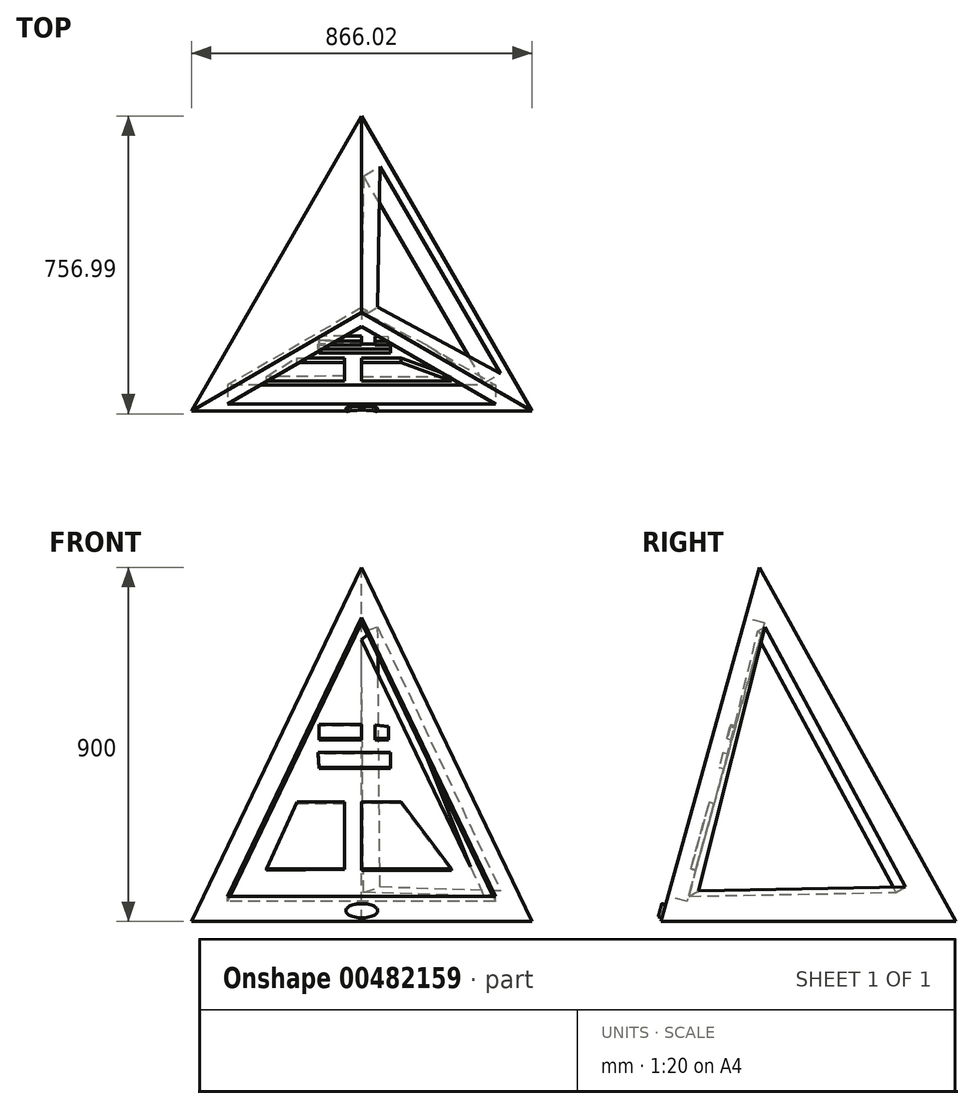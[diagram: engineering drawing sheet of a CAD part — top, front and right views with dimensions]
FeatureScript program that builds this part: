
annotation { "Feature Type Name" : "Feature", "Feature Type Description" : "" }
export const myFeature = defineFeature(function(context is Context, id is Id, definition is map)
    precondition{}
    {
        {
            var Q0;
            Q0=qCreatedBy(makeId("Top.planeOp"),FACE);
            var sketch = newSketch(context, id + "F0", { "sketchPlane" : qUnion([Q0])});
            skCircle(sketch, "E0.cCircle", {"center": v(0, 0) * mm, "radius": 250 * mm, "construction": true});
            skLineSegment(sketch, "E0.0", {"start": v(433.01, -250) * mm, "end": v(-433.01, -250) * mm});
            skLineSegment(sketch, "E0.1", {"start": v(-433.01, -250) * mm, "end": v(0, 500) * mm});
            skLineSegment(sketch, "E0.2", {"start": v(0, 500) * mm, "end": v(433.01, -250) * mm});
            skPoint(sketch, "E0.0.midPoint", {"position": v(0, -250) * mm});
            skSolve(sketch);
        }
        {
            var Q0;
            Q0=qCreatedBy(makeId("Top.planeOp"),FACE);
            cPlane(context, id + "F1", {"entities" : qUnion([Q0]), "cplaneType" : CPlaneType.OFFSET, "offset" : 400 * mm, "width" : 152.4 * mm, "height" : 152.4 * mm});
        }
        {
            var Q0;
            Q0=qCreatedBy(id+"F1.planeOp",FACE);
            cPlane(context, id + "F2", {"entities" : qUnion([Q0]), "cplaneType" : CPlaneType.OFFSET, "offset" : 500 * mm, "width" : 152.4 * mm, "height" : 152.4 * mm});
        }
        {
            var Q0;
            Q0=qCreatedBy(id+"F2.planeOp",FACE);
            var sketch = newSketch(context, id + "F3", { "sketchPlane" : qUnion([Q0])});
            skPoint(sketch, "E1.0", {"position": v(0, 0) * mm});
            skSolve(sketch);
        }
        {
            var Q0;
            Q0=makeQuery(id+"F0.imprint","IMPRINT",FACE,{"disambiguationData":[TD([[makeQuery(id+"F0.imprint","IMPRINT",EDGE,{"derivedFrom":sQuery(id+"F0.wireOp",EDGE,"E0.0")}),-1.0]])]});
            var Q1;
            Q1=sQuery(id+"F3.wireOp",VERTEX,"E1.0");
            loft(context, id + "F4", {"sheetProfilesArray" : [{ "sheetProfileEntities" : qUnion([Q0]) }, { "sheetProfileEntities" : qUnion([Q1]) }]});
        }
        {
            var Q0;
            {var subQ0=sQuery(id+"F0.wireOp",EDGE,"E0.0");var subQ1=sQuery(id+"F0.wireOp",EDGE,"E0.1");var subQ2=sQuery(id+"F0.wireOp",EDGE,"E0.2");Q0=makeQuery(id+"F4.opLoft","SWEPT_FACE",FACE,{"disambiguationData":[OSD([subQ0,subQ1,subQ2]),TDD([makeQuery(id+"F0.imprint","INTERSECT",VERTEX,{"derivedFrom":[subQ0,subQ2]}),makeQuery(id+"F0.imprint","INTERSECT",VERTEX,{"derivedFrom":[subQ0,subQ1]}),makeQuery(id+"F0.imprint","IMPRINT",EDGE,{"derivedFrom":subQ0})])]});}
            var sketch = newSketch(context, id + "F5", { "sketchPlane" : qUnion([Q0])});
            skLineSegment(sketch, "E2", {"start": v(0, 734.6) * mm, "end": v(-340.54, 0) * mm});
            skLineSegment(sketch, "E3", {"start": v(0, 734.6) * mm, "end": v(339.74, 0) * mm});
            skLineSegment(sketch, "E4", {"start": v(339.74, 0) * mm, "end": v(-340.54, 0) * mm});
            skSolve(sketch);
        }
        {
            var Q0;
            Q0 = qSketchRegion(id + "F5", true);
            extrude(context, id + "F6", {"entities" : qUnion([Q0]), "operationType" : NewBodyOperationType.REMOVE, "oppositeDirection" : true, "depth" : 50 * mm});
        }
        {
            var Q0;
            {var subQ0=sQuery(id+"F0.wireOp",EDGE,"E0.2");var subQ1=sQuery(id+"F0.wireOp",EDGE,"E0.1");var subQ2=sQuery(id+"F0.wireOp",EDGE,"E0.0");Q0=makeQuery(id+"F4.opLoft","SWEPT_FACE",FACE,{"disambiguationData":[OSD([subQ2,subQ1,subQ0]),TDD([makeQuery(id+"F0.imprint","INTERSECT",VERTEX,{"derivedFrom":[subQ2,subQ0]}),makeQuery(id+"F0.imprint","INTERSECT",VERTEX,{"derivedFrom":[subQ1,subQ0]}),makeQuery(id+"F0.imprint","IMPRINT",EDGE,{"derivedFrom":subQ0})])]});}
            var sketch = newSketch(context, id + "F7", { "sketchPlane" : qUnion([Q0])});
            skLineSegment(sketch, "E5", {"start": v(-116.62, 700.24) * mm, "end": v(-308.34, -33.85) * mm});
            skLineSegment(sketch, "E6", {"start": v(-308.34, -33.85) * mm, "end": v(291.14, 69.38) * mm});
            skLineSegment(sketch, "E7", {"start": v(291.14, 69.38) * mm, "end": v(-116.62, 700.24) * mm});
            skSolve(sketch);
        }
        {
            var Q0;
            Q0 = qSketchRegion(id + "F7", true);
            extrude(context, id + "F8", {"entities" : qUnion([Q0]), "operationType" : NewBodyOperationType.REMOVE, "oppositeDirection" : true, "depth" : 50 * mm});
        }
        {
            var Q0;
            Q0=makeQuery(id+"F6.boolean.opBoolean","COPY",FACE,{"derivedFrom":makeQuery(id+"F6.opExtrude","CAP_FACE",FACE,{"disambiguationData":[OSD([sQuery(id+"F5.wireOp",EDGE,"E2"),sQuery(id+"F5.wireOp",EDGE,"E3"),sQuery(id+"F5.wireOp",EDGE,"E4")])],"isStart":false})});
            var sketch = newSketch(context, id + "F9", { "sketchPlane" : qUnion([Q0])});
            skLineSegment(sketch, "E8", {"start": v(-241.35, 82.39) * mm, "end": v(-164.87, 258.78) * mm});
            skLineSegment(sketch, "E9", {"start": v(-164.87, 258.78) * mm, "end": v(-44.2, 258.78) * mm});
            skLineSegment(sketch, "E10", {"start": v(-44.2, 258.78) * mm, "end": v(-44.2, 84.15) * mm});
            skLineSegment(sketch, "E11", {"start": v(-44.2, 84.15) * mm, "end": v(-241.35, 82.39) * mm});
            skLineSegment(sketch, "E12", {"start": v(0, 258.78) * mm, "end": v(0, 82.39) * mm});
            skLineSegment(sketch, "E13", {"start": v(0, 82.39) * mm, "end": v(227.75, 82.39) * mm});
            skLineSegment(sketch, "E14", {"start": v(227.75, 82.39) * mm, "end": v(100.28, 258.78) * mm});
            skLineSegment(sketch, "E15", {"start": v(100.28, 258.78) * mm, "end": v(0, 258.78) * mm});
            skLineSegment(sketch, "E16", {"start": v(-108.78, 350.51) * mm, "end": v(73.08, 350.51) * mm});
            skLineSegment(sketch, "E17", {"start": v(73.08, 350.51) * mm, "end": v(73.08, 389.32) * mm});
            skLineSegment(sketch, "E18", {"start": v(73.08, 389.32) * mm, "end": v(-110.48, 389.32) * mm});
            skLineSegment(sketch, "E19", {"start": v(-110.48, 389.32) * mm, "end": v(-108.78, 350.51) * mm});
            skLineSegment(sketch, "E20", {"start": v(-108.78, 426.36) * mm, "end": v(0, 426.36) * mm});
            skLineSegment(sketch, "E21", {"start": v(0, 426.36) * mm, "end": v(0, 463.4) * mm});
            skLineSegment(sketch, "E22", {"start": v(0, 463.4) * mm, "end": v(-108.78, 463.4) * mm});
            skLineSegment(sketch, "E23", {"start": v(-108.78, 463.4) * mm, "end": v(-108.78, 426.36) * mm});
            skLineSegment(sketch, "E24", {"start": v(34, 461.64) * mm, "end": v(34, 426.36) * mm});
            skLineSegment(sketch, "E25", {"start": v(34, 426.36) * mm, "end": v(67.99, 426.36) * mm});
            skLineSegment(sketch, "E26", {"start": v(67.99, 426.36) * mm, "end": v(67.99, 458.12) * mm});
            skLineSegment(sketch, "E27", {"start": v(67.99, 458.12) * mm, "end": v(34, 461.64) * mm});
            skSolve(sketch);
        }
        {
            var Q0;
            {var subQ0=sQuery(id+"F0.wireOp",EDGE,"E0.0");var subQ1=sQuery(id+"F0.wireOp",EDGE,"E0.1");var subQ2=sQuery(id+"F0.wireOp",EDGE,"E0.2");Q0=makeQuery(id+"F4.opLoft","SWEPT_FACE",FACE,{"disambiguationData":[OSD([subQ0,subQ1,subQ2]),TDD([makeQuery(id+"F0.imprint","INTERSECT",VERTEX,{"derivedFrom":[subQ0,subQ2]}),makeQuery(id+"F0.imprint","INTERSECT",VERTEX,{"derivedFrom":[subQ0,subQ1]}),makeQuery(id+"F0.imprint","IMPRINT",EDGE,{"derivedFrom":subQ0})])]});}
            var sketch = newSketch(context, id + "F10", { "sketchPlane" : qUnion([Q0])});
            skEllipse(sketch, "E28", {"center": v(0, -39.74) * mm, "majorRadius": 40.13 * mm, "minorRadius": 17.28 * mm, "majorAxis": v(1, 0)});
            skSolve(sketch);
        }
        {
            var Q0;
            Q0 = qSketchRegion(id + "F10", true);
            extrude(context, id + "F11", {"entities" : qUnion([Q0]), "operationType" : NewBodyOperationType.ADD, "depth" : 10 * mm});
        }
        {
            var Q0;
            Q0=makeQuery(id+"F9.imprint","IMPRINT",FACE,{"disambiguationData":[TD([[makeQuery(id+"F9.imprint","IMPRINT",EDGE,{"derivedFrom":sQuery(id+"F9.wireOp",EDGE,"E8")}),-1.0]])]});
            var Q1;
            Q1=makeQuery(id+"F9.imprint","IMPRINT",FACE,{"disambiguationData":[TD([[makeQuery(id+"F9.imprint","IMPRINT",EDGE,{"derivedFrom":sQuery(id+"F9.wireOp",EDGE,"E12")}),1.0]])]});
            var Q2;
            Q2=makeQuery(id+"F9.imprint","IMPRINT",FACE,{"disambiguationData":[TD([[makeQuery(id+"F9.imprint","IMPRINT",EDGE,{"derivedFrom":sQuery(id+"F9.wireOp",EDGE,"E16")}),1.0]])]});
            var Q3;
            Q3=makeQuery(id+"F9.imprint","IMPRINT",FACE,{"disambiguationData":[TD([[makeQuery(id+"F9.imprint","IMPRINT",EDGE,{"derivedFrom":sQuery(id+"F9.wireOp",EDGE,"E20")}),1.0]])]});
            var Q4;
            Q4=makeQuery(id+"F9.imprint","IMPRINT",FACE,{"disambiguationData":[TD([[makeQuery(id+"F9.imprint","IMPRINT",EDGE,{"derivedFrom":sQuery(id+"F9.wireOp",EDGE,"E24")}),1.0]])]});
            extrude(context, id + "F12", {"entities" : qUnion([Q0, Q1, Q2, Q3, Q4]), "operationType" : NewBodyOperationType.ADD, "depth" : 12.7 * mm});
        }
    });
